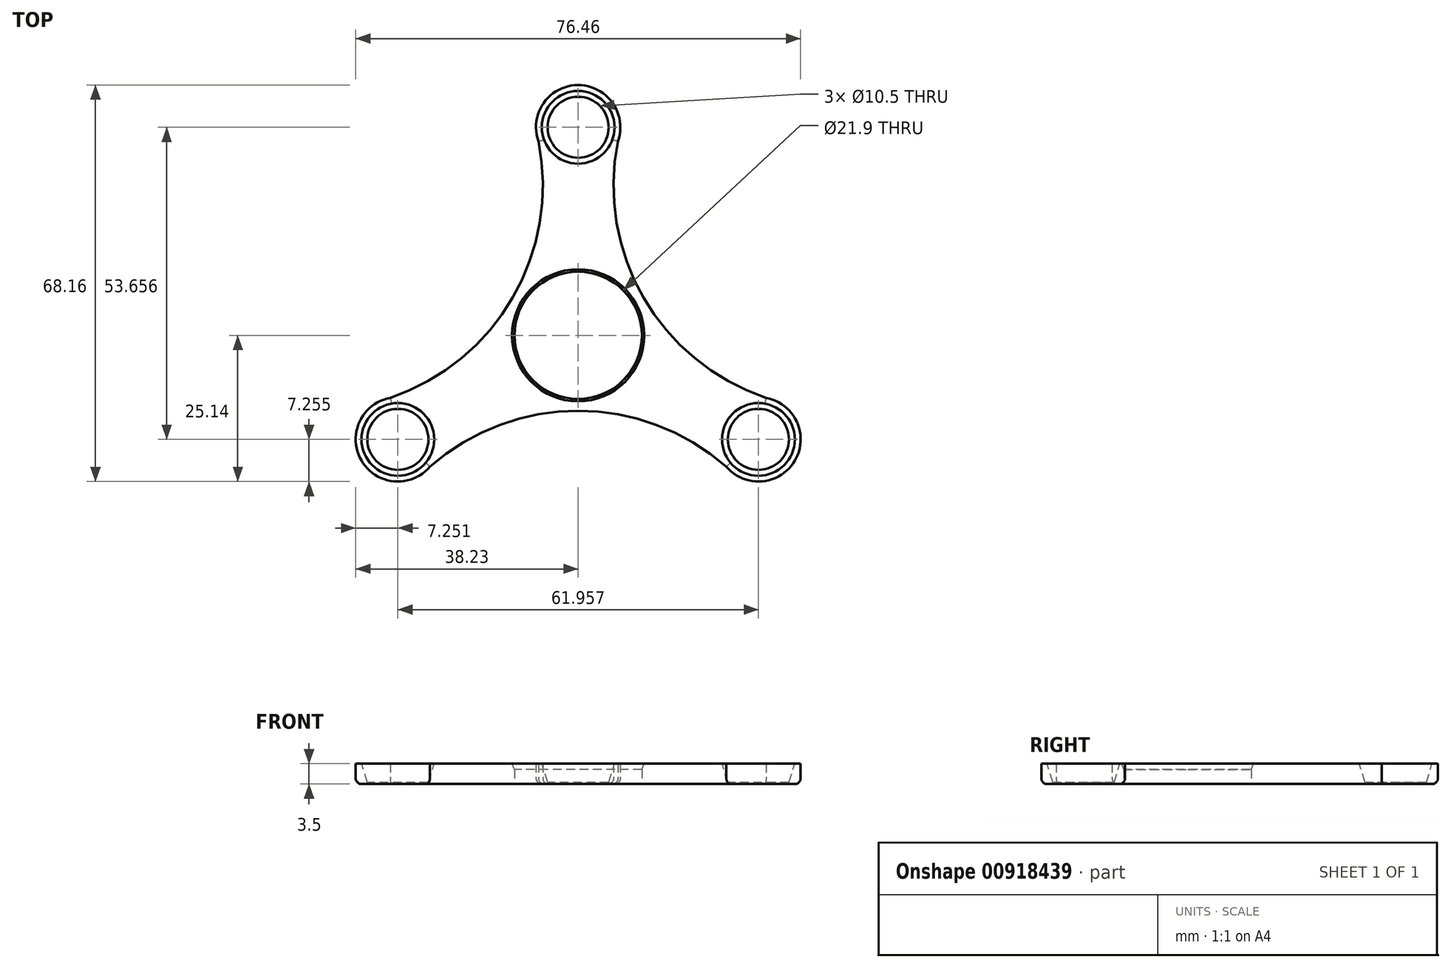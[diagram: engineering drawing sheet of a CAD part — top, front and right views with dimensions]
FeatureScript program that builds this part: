
annotation { "Feature Type Name" : "Feature", "Feature Type Description" : "" }
export const myFeature = defineFeature(function(context is Context, id is Id, definition is map)
    precondition{}
    {
        {
            var Q0;
            Q0=qCreatedBy(makeId("Top.planeOp"),FACE);
            var sketch = newSketch(context, id + "F0", { "sketchPlane" : qUnion([Q0])});
            skCircle(sketch, "E0", {"center": v(0, 0) * mm, "radius": 10.95 * mm});
            skCircle(sketch, "E1", {"center": v(0, 35.77) * mm, "radius": 5.25 * mm});
            skArc(sketch, "E2", {"start": v(6.83, 33.35) * mm, "mid": v(0, 43.02) * mm, "end": v(-6.83, 33.35) * mm});
            skArc(sketch, "E3.1.0", {"start": v(-32.3, -10.76) * mm, "mid": v(-37.26, -21.51) * mm, "end": v(-25.47, -22.6) * mm});
            skCircle(sketch, "E3.1.1", {"center": v(-30.98, -17.89) * mm, "radius": 5.25 * mm});
            skArc(sketch, "E3.2.0", {"start": v(25.47, -22.6) * mm, "mid": v(37.26, -21.51) * mm, "end": v(32.3, -10.76) * mm});
            skCircle(sketch, "E3.2.1", {"center": v(30.98, -17.89) * mm, "radius": 5.25 * mm});
            skArc(sketch, "E4", {"start": v(-32.3, -10.76) * mm, "mid": v(-11.24, 6.49) * mm, "end": v(-6.83, 33.35) * mm});
            skArc(sketch, "E5.1.0", {"start": v(25.47, -22.6) * mm, "mid": v(0, -12.98) * mm, "end": v(-25.47, -22.6) * mm});
            skArc(sketch, "E5.2.0", {"start": v(6.83, 33.35) * mm, "mid": v(11.24, 6.49) * mm, "end": v(32.3, -10.76) * mm});
            skPoint(sketch, "E6.orphan", {"position": v(33.95, -11.27) * mm});
            skPoint(sketch, "E7.orphan", {"position": v(26.74, -23.76) * mm});
            skPoint(sketch, "E8.orphan", {"position": v(-33.95, -11.27) * mm});
            skPoint(sketch, "E9.orphan", {"position": v(-26.74, -23.76) * mm});
            skPoint(sketch, "E10.orphan", {"position": v(-7.21, 35.04) * mm});
            skPoint(sketch, "E11.orphan", {"position": v(7.21, 35.04) * mm});
            skSolve(sketch);
        }
        {
            var Q0;
            Q0=makeQuery(id+"F0.imprint","IMPRINT",FACE,{"disambiguationData":[TD([[makeQuery(id+"F0.imprint","IMPRINT",EDGE,{"derivedFrom":sQuery(id+"F0.wireOp",EDGE,"E0")}),-1.0]])]});
            extrude(context, id + "F1", {"entities" : qUnion([Q0]), "depth" : 3.5 * mm, "offsetDistance" : 25 * mm});
        }
        {
            var Q0;
            Q0=makeQuery(id+"F1.opExtrude","CAP_EDGE",EDGE,{"disambiguationData":[OSD([sQuery(id+"F0.wireOp",EDGE,"E0")])],"isStart":false});
            chamfer(context, id + "F2", {"entities" : qUnion([Q0]), "chamferType" : ChamferType.TWO_OFFSETS, "width1" : 1 * mm, "oppositeDirection" : false, "width2" : .4 * mm, "tangentPropagation" : true});
        }
        {
            var Q0;
            Q0=makeQuery(id+"F1.opExtrude","CAP_EDGE",EDGE,{"disambiguationData":[OSD([sQuery(id+"F0.wireOp",EDGE,"E1")])],"isStart":false});
            var Q1;
            Q1=makeQuery(id+"F1.opExtrude","CAP_EDGE",EDGE,{"disambiguationData":[OSD([sQuery(id+"F0.wireOp",EDGE,"E3.1.1")])],"isStart":false});
            var Q2;
            Q2=makeQuery(id+"F1.opExtrude","CAP_EDGE",EDGE,{"disambiguationData":[OSD([sQuery(id+"F0.wireOp",EDGE,"E3.2.1")])],"isStart":false});
            chamfer(context, id + "F3", {"entities" : qUnion([Q0, Q1, Q2]), "chamferType" : ChamferType.TWO_OFFSETS, "width1" : 3.2 * mm, "oppositeDirection" : false, "width2" : 1 * mm, "tangentPropagation" : true});
        }
        {
            var Q0;
            Q0=makeQuery(id+"F1.opExtrude","CAP_EDGE",EDGE,{"disambiguationData":[OSD([sQuery(id+"F0.wireOp",EDGE,"E5.1.0")])],"isStart":true});
            var Q1;
            Q1=makeQuery(id+"F1.opExtrude","CAP_EDGE",EDGE,{"disambiguationData":[OSD([sQuery(id+"F0.wireOp",EDGE,"E5.2.0")])],"isStart":true});
            var Q2;
            Q2=makeQuery(id+"F1.opExtrude","CAP_EDGE",EDGE,{"disambiguationData":[OSD([sQuery(id+"F0.wireOp",EDGE,"E3.2.0")])],"isStart":true});
            var Q3;
            Q3=makeQuery(id+"F1.opExtrude","CAP_EDGE",EDGE,{"disambiguationData":[OSD([sQuery(id+"F0.wireOp",EDGE,"E2")])],"isStart":true});
            var Q4;
            Q4=makeQuery(id+"F1.opExtrude","CAP_EDGE",EDGE,{"disambiguationData":[OSD([sQuery(id+"F0.wireOp",EDGE,"E3.1.0")])],"isStart":true});
            var Q5;
            Q5=makeQuery(id+"F1.opExtrude","CAP_EDGE",EDGE,{"disambiguationData":[OSD([sQuery(id+"F0.wireOp",EDGE,"E4")])],"isStart":true});
            fillet(context, id + "F4", {"entities" : qUnion([Q0, Q1, Q2, Q3, Q4, Q5]), "radius" : 1 * mm, "tangentPropagation" : true, "allowEdgeOverflow" : false});
        }
    });
